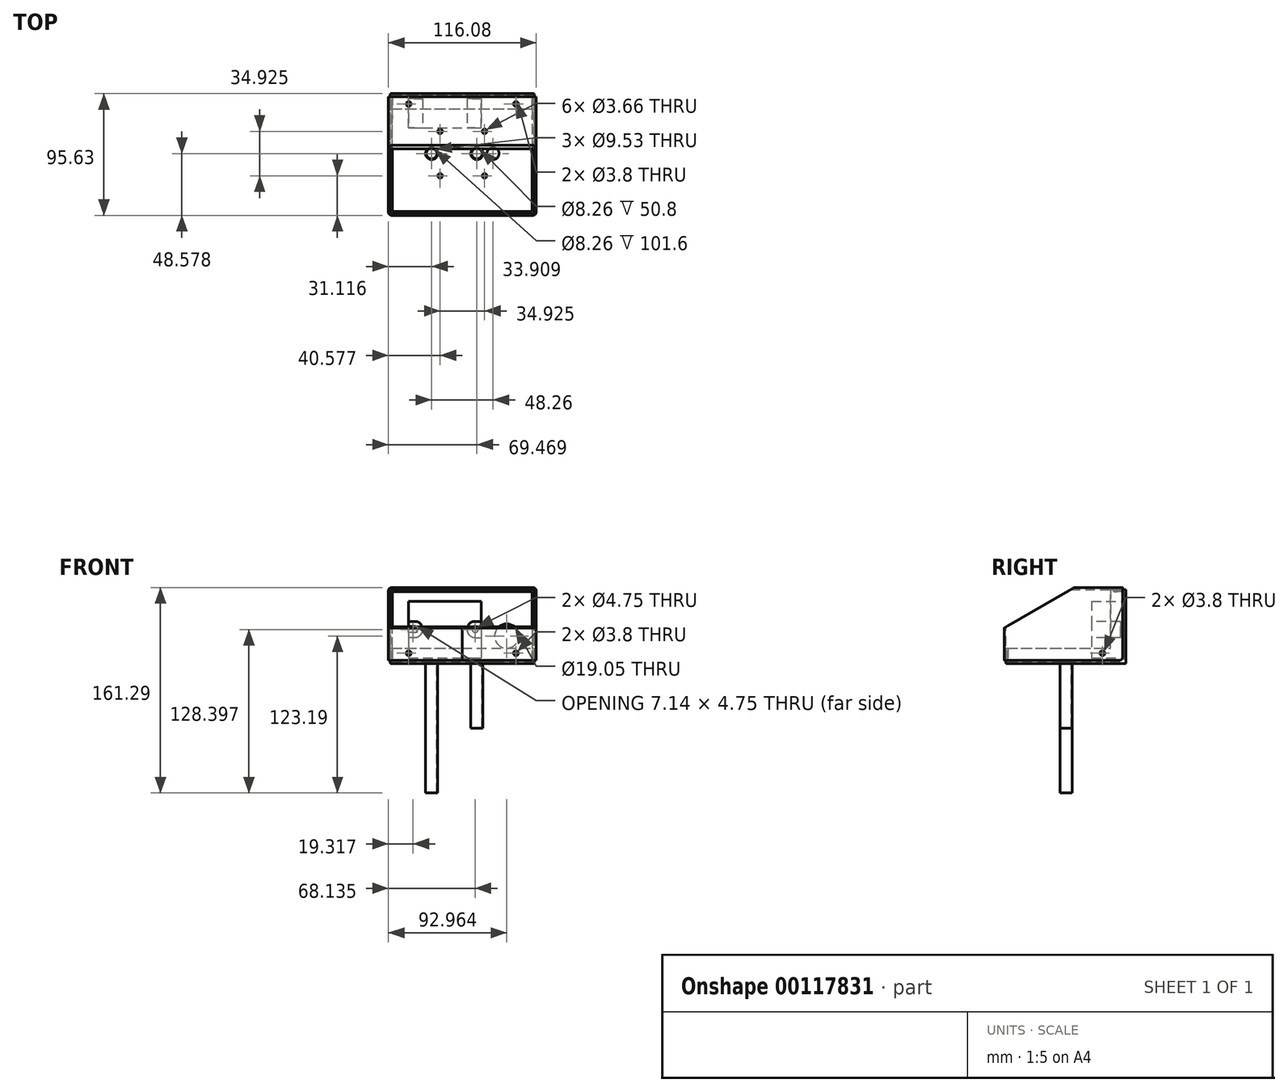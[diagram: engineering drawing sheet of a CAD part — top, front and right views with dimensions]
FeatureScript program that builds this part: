
annotation { "Feature Type Name" : "Feature", "Feature Type Description" : "" }
export const myFeature = defineFeature(function(context is Context, id is Id, definition is map)
    precondition{}
    {
        {
            var Q0;
            Q0=qCreatedBy(makeId("Right.planeOp"),FACE);
            var sketch = newSketch(context, id + "F0", { "sketchPlane" : qUnion([Q0])});
            skLineSegment(sketch, "E0", {"start": v(0, 0) * mm, "end": v(0, 25.4) * mm});
            skLineSegment(sketch, "E1", {"start": v(0, 25.4) * mm, "end": v(55, 57.15) * mm});
            skLineSegment(sketch, "E2", {"start": v(55, 57.15) * mm, "end": v(93.1, 57.15) * mm});
            skLineSegment(sketch, "E3", {"start": v(93.1, 57.15) * mm, "end": v(93.1, 0) * mm});
            skLineSegment(sketch, "E4", {"start": v(93.1, 0) * mm, "end": v(0, 0) * mm});
            skSolve(sketch);
        }
        {
            var Q0;
            Q0 = qSketchRegion(id + "F0", true);
            extrude(context, id + "F1", {"entities" : qUnion([Q0]), "depth" : 116.08 * mm});
        }
        {
            var Q0;
            Q0=makeQuery(id+"F1.opExtrude","CAP_EDGE",EDGE,{"disambiguationData":[OSD([sQuery(id+"F0.wireOp",EDGE,"E2")])],"isStart":false});
            var Q1;
            Q1=makeQuery(id+"F1.opExtrude","CAP_EDGE",EDGE,{"disambiguationData":[OSD([sQuery(id+"F0.wireOp",EDGE,"E0")])],"isStart":false});
            var Q2;
            Q2=makeQuery(id+"F1.opExtrude","CAP_EDGE",EDGE,{"disambiguationData":[OSD([sQuery(id+"F0.wireOp",EDGE,"E0")])],"isStart":true});
            var Q3;
            Q3=makeQuery(id+"F1.opExtrude","CAP_EDGE",EDGE,{"disambiguationData":[OSD([sQuery(id+"F0.wireOp",EDGE,"E2")])],"isStart":true});
            fillet(context, id + "F2", {"entities" : qUnion([Q0, Q1, Q2, Q3]), "radius" : 2.54 * mm, "tangentPropagation" : true, "allowEdgeOverflow" : false});
        }
        {
            var Q0;
            Q0=makeQuery(id+"F1.opExtrude","SWEPT_FACE",FACE,{"disambiguationData":[OSD([sQuery(id+"F0.wireOp",EDGE,"E3")])]});
            var Q1;
            Q1=makeQuery(id+"F1.opExtrude","SWEPT_FACE",FACE,{"disambiguationData":[OSD([sQuery(id+"F0.wireOp",EDGE,"E4")])]});
            var Q2;
            Q2=makeQuery(id+"F1.opExtrude","SWEPT_FACE",FACE,{"disambiguationData":[OSD([sQuery(id+"F0.wireOp",EDGE,"E1")])]});
            shell(context, id + "F3", {"entities" : qUnion([Q0, Q1, Q2]), "thickness" : 1.52 * mm});
        }
        {
            var Q0;
            {var subQ0=sQuery(id+"F0.wireOp",EDGE,"E4");var subQ1=sQuery(id+"F0.wireOp",EDGE,"E3");var subQ2=sQuery(id+"F0.wireOp",EDGE,"E2");var subQ3=sQuery(id+"F0.wireOp",EDGE,"E1");var subQ4=sQuery(id+"F0.wireOp",EDGE,"E0");Q0=makeQuery(id+"F3.opShell","OFFSET_FACE",FACE,{"disambiguationData":[OSD([subQ4,subQ3,subQ2,subQ1,subQ0]),TDD([makeQuery(id+"F1.opExtrude","CAP_FACE",FACE,{"disambiguationData":[OSD([subQ4,subQ3,subQ2,subQ1,subQ0])],"isStart":false})])]});}
            var sketch = newSketch(context, id + "F4", { "sketchPlane" : qUnion([Q0])});
            skLineSegment(sketch, "E5.0", {"start": v(-93.1, 0) * mm, "end": v(-1.52, 0) * mm, "construction": true});
            skLineSegment(sketch, "E5.1", {"start": v(-93.1, 55.63) * mm, "end": v(-93.1, 0) * mm, "construction": true});
            skLineSegment(sketch, "E6.0", {"start": v(-83.57, 9.53) * mm, "end": v(-1.52, 9.53) * mm});
            skLineSegment(sketch, "E6.1", {"start": v(-83.57, 55.63) * mm, "end": v(-83.57, 9.53) * mm});
            skLineSegment(sketch, "E7", {"start": v(-83.57, 55.63) * mm, "end": v(-93.1, 55.63) * mm});
            skLineSegment(sketch, "E8", {"start": v(-1.52, 0) * mm, "end": v(-1.52, 9.53) * mm});
            skLineSegment(sketch, "E9.0", {"start": v(-95.63, -2.54) * mm, "end": v(-1.52, -2.54) * mm});
            skLineSegment(sketch, "E9.1", {"start": v(-95.63, 55.63) * mm, "end": v(-95.63, -2.54) * mm});
            skLineSegment(sketch, "E10", {"start": v(-95.63, 55.63) * mm, "end": v(-93.1, 55.63) * mm});
            skLineSegment(sketch, "E11", {"start": v(-1.52, -2.54) * mm, "end": v(-1.52, 0) * mm});
            skSolve(sketch);
        }
        {
            var Q0;
            Q0 = qSketchRegion(id + "F4", true);
            var Q1;
            {var subQ0=sQuery(id+"F0.wireOp",EDGE,"E4");var subQ1=sQuery(id+"F0.wireOp",EDGE,"E3");var subQ2=sQuery(id+"F0.wireOp",EDGE,"E2");var subQ3=sQuery(id+"F0.wireOp",EDGE,"E1");var subQ4=sQuery(id+"F0.wireOp",EDGE,"E0");Q1=makeQuery(id+"F3.opShell","OFFSET_FACE",FACE,{"disambiguationData":[OSD([subQ4,subQ3,subQ2,subQ1,subQ0]),TDD([makeQuery(id+"F1.opExtrude","CAP_FACE",FACE,{"disambiguationData":[OSD([subQ4,subQ3,subQ2,subQ1,subQ0])],"isStart":true})])]});}
            var Q2;
            Q2=makeQuery(id+"F1.opExtrude","SWEPT_BODY",BODY,{"disambiguationData":[OSD([sQuery(id+"F0.wireOp",EDGE,"E0"),sQuery(id+"F0.wireOp",EDGE,"E1"),sQuery(id+"F0.wireOp",EDGE,"E2"),sQuery(id+"F0.wireOp",EDGE,"E3"),sQuery(id+"F0.wireOp",EDGE,"E4")])]});
            extrude(context, id + "F5", {"entities" : qUnion([Q0]), "endBound" : BoundingType.UP_TO_SURFACE, "endBoundEntityFace" : qUnion([Q1]), "endBoundEntityBody" : qUnion([Q2]), "depth" : 25.4 * mm});
        }
        {
            var Q0;
            Q0=makeQuery(id+"F5.opExtrude","SWEPT_FACE",FACE,{"disambiguationData":[OSD([sQuery(id+"F4.wireOp",EDGE,"E6.1")])]});
            var Q1;
            Q1=makeQuery(id+"F5.opExtrude","SWEPT_FACE",FACE,{"disambiguationData":[OSD([sQuery(id+"F4.wireOp",EDGE,"E6.0")])]});
            shell(context, id + "F6", {"entities" : qUnion([Q0, Q1]), "thickness" : 1.52 * mm});
        }
        {
            var Q0;
            {var subQ0=sQuery(id+"F4.wireOp",EDGE,"E9.1");Q0=makeQuery(id+"F6.opShell","OFFSET_FACE",FACE,{"disambiguationData":[OSD([subQ0]),TDD([makeQuery(id+"F5.opExtrude","SWEPT_FACE",FACE,{"disambiguationData":[OSD([subQ0])]})])]});}
            var sketch = newSketch(context, id + "F7", { "sketchPlane" : qUnion([Q0])});
            skLineSegment(sketch, "E12.bottom", {"start": v(15.75, 46.48) * mm, "end": v(72.9, 46.48) * mm});
            skLineSegment(sketch, "E12.top", {"start": v(15.75, 2.03) * mm, "end": v(72.9, 2.03) * mm});
            skLineSegment(sketch, "E12.left", {"start": v(15.75, 46.48) * mm, "end": v(15.75, 2.03) * mm});
            skLineSegment(sketch, "E12.right", {"start": v(72.9, 46.48) * mm, "end": v(72.9, 2.03) * mm});
            skSolve(sketch);
        }
        {
            var Q0;
            Q0 = qSketchRegion(id + "F7", true);
            extrude(context, id + "F8", {"entities" : qUnion([Q0]), "depth" : 25.4 * mm});
        }
        {
            var Q0;
            Q0=makeQuery(id+"F8.opExtrude","CAP_FACE",FACE,{"disambiguationData":[OSD([sQuery(id+"F7.wireOp",EDGE,"E12.bottom"),sQuery(id+"F7.wireOp",EDGE,"E12.top"),sQuery(id+"F7.wireOp",EDGE,"E12.left"),sQuery(id+"F7.wireOp",EDGE,"E12.right")])],"isStart":false});
            var sketch = newSketch(context, id + "F9", { "sketchPlane" : qUnion([Q0])});
            skArc(sketch, "E13", {"start": v(68.14, 30.6) * mm, "mid": v(61.79, 24.26) * mm, "end": v(68.14, 17.9) * mm});
            skPoint(sketch, "E13.centerSnap0", {"position": v(72.9, 24.26) * mm});
            skLineSegment(sketch, "E14", {"start": v(44.32, 46.48) * mm, "end": v(44.32, 2.03) * mm, "construction": true});
            skLineSegment(sketch, "E15", {"start": v(68.14, 30.6) * mm, "end": v(72.9, 30.6) * mm});
            skLineSegment(sketch, "E16", {"start": v(68.14, 17.9) * mm, "end": v(72.9, 17.9) * mm});
            skLineSegment(sketch, "E17", {"start": v(72.9, 17.9) * mm, "end": v(72.9, 30.6) * mm});
            skLineSegment(sketch, "E18.MirrorCS", {"start": v(20.51, 30.6) * mm, "end": v(15.75, 30.6) * mm});
            skLineSegment(sketch, "E19.MirrorCS", {"start": v(20.51, 17.9) * mm, "end": v(15.75, 17.9) * mm});
            skLineSegment(sketch, "E20.MirrorCS", {"start": v(15.75, 17.9) * mm, "end": v(15.75, 30.6) * mm});
            skArc(sketch, "E21.MirrorCS", {"start": v(20.51, 30.6) * mm, "mid": v(26.86, 24.26) * mm, "end": v(20.51, 17.9) * mm});
            skSolve(sketch);
        }
        {
            var Q0;
            Q0 = qSketchRegion(id + "F9", true);
            extrude(context, id + "F10", {"entities" : qUnion([Q0]), "operationType" : NewBodyOperationType.REMOVE, "oppositeDirection" : true, "depth" : 22.86 * mm});
        }
        {
            var Q0;
            Q0=makeQuery(id+"F8.opExtrude","CAP_FACE",FACE,{"disambiguationData":[OSD([sQuery(id+"F7.wireOp",EDGE,"E12.bottom"),sQuery(id+"F7.wireOp",EDGE,"E12.top"),sQuery(id+"F7.wireOp",EDGE,"E12.left"),sQuery(id+"F7.wireOp",EDGE,"E12.right")])],"isStart":false});
            var sketch = newSketch(context, id + "F11", { "sketchPlane" : qUnion([Q0])});
            skArc(sketch, "E22", {"start": v(20.51, 21.88) * mm, "mid": v(22.89, 24.26) * mm, "end": v(20.51, 26.63) * mm});
            skLineSegment(sketch, "E23", {"start": v(20.51, 26.63) * mm, "end": v(15.75, 26.63) * mm});
            skLineSegment(sketch, "E24", {"start": v(20.51, 21.88) * mm, "end": v(15.75, 21.88) * mm});
            skLineSegment(sketch, "E25", {"start": v(15.75, 21.88) * mm, "end": v(15.75, 26.63) * mm});
            skCircle(sketch, "E26", {"center": v(68.14, 24.26) * mm, "radius": 2.37 * mm});
            skSolve(sketch);
        }
        {
            var Q0;
            Q0 = qSketchRegion(id + "F11", true);
            extrude(context, id + "F12", {"entities" : qUnion([Q0]), "operationType" : NewBodyOperationType.REMOVE, "endBound" : BoundingType.THROUGH_ALL, "oppositeDirection" : true, "depth" : 25.4 * mm});
        }
        {
            var Q0;
            Q0=makeQuery(id+"F5.opExtrude","SWEPT_FACE",FACE,{"disambiguationData":[OSD([sQuery(id+"F4.wireOp",EDGE,"E9.0")])]});
            var sketch = newSketch(context, id + "F13", { "sketchPlane" : qUnion([Q0])});
            skCircle(sketch, "E27", {"center": v(82.17, -48.58) * mm, "radius": 4.76 * mm});
            skCircle(sketch, "E28", {"center": v(69.47, -48.58) * mm, "radius": 4.76 * mm});
            skLineSegment(sketch, "E29", {"start": v(58.04, -93.1) * mm, "end": v(58.04, -4.06) * mm, "construction": true});
            skCircle(sketch, "E30", {"center": v(33.9, -48.58) * mm, "radius": 4.76 * mm});
            skPoint(sketch, "E31", {"position": v(58.04, -48.58) * mm});
            skSolve(sketch);
        }
        {
            var Q0;
            Q0 = qSketchRegion(id + "F13", true);
            extrude(context, id + "F14", {"entities" : qUnion([Q0]), "operationType" : NewBodyOperationType.REMOVE, "endBound" : BoundingType.UP_TO_NEXT, "oppositeDirection" : true, "depth" : 25.4 * mm});
        }
        {
            var Q0;
            Q0=makeQuery(id+"F5.opExtrude","SWEPT_FACE",FACE,{"disambiguationData":[OSD([sQuery(id+"F4.wireOp",EDGE,"E9.0")])]});
            var sketch = newSketch(context, id + "F15", { "sketchPlane" : qUnion([Q0])});
            skCircle(sketch, "E32.0", {"center": v(33.9, -48.58) * mm, "radius": 4.76 * mm});
            skCircle(sketch, "E32.1", {"center": v(69.47, -48.58) * mm, "radius": 4.76 * mm});
            skCircle(sketch, "E33.0", {"center": v(69.47, -48.58) * mm, "radius": 4.13 * mm});
            skCircle(sketch, "E34.0", {"center": v(33.9, -48.58) * mm, "radius": 4.13 * mm});
            skSolve(sketch);
        }
        {
            var Q0;
            Q0=makeQuery(id+"F15.imprint","IMPRINT",FACE,{"disambiguationData":[TD([[makeQuery(id+"F15.imprint","IMPRINT",EDGE,{"derivedFrom":sQuery(id+"F15.wireOp",EDGE,"E32.1")}),1.0]])]});
            extrude(context, id + "F16", {"entities" : qUnion([Q0]), "depth" : 50.8 * mm});
        }
        {
            var Q0;
            Q0=makeQuery(id+"F15.imprint","IMPRINT",FACE,{"disambiguationData":[TD([[makeQuery(id+"F15.imprint","IMPRINT",EDGE,{"derivedFrom":sQuery(id+"F15.wireOp",EDGE,"E32.0")}),1.0]])]});
            extrude(context, id + "F17", {"entities" : qUnion([Q0]), "depth" : 101.6 * mm});
        }
        {
            var Q0;
            Q0=makeQuery(id+"F13.imprint","IMPRINT",FACE,{"disambiguationData":[TD([[makeQuery(id+"F13.imprint","IMPRINT",EDGE,{"derivedFrom":sQuery(id+"F13.wireOp",EDGE,"E27")}),-1.0]])]});
            var sketch = newSketch(context, id + "F18", { "sketchPlane" : qUnion([Q0])});
            skLineSegment(sketch, "E35.bottom", {"start": v(75.5, -66.04) * mm, "end": v(40.58, -66.04) * mm, "construction": true});
            skLineSegment(sketch, "E35.top", {"start": v(75.5, -31.12) * mm, "end": v(40.58, -31.12) * mm, "construction": true});
            skLineSegment(sketch, "E35.left", {"start": v(75.5, -66.04) * mm, "end": v(75.5, -31.12) * mm, "construction": true});
            skLineSegment(sketch, "E35.right", {"start": v(40.58, -66.04) * mm, "end": v(40.58, -31.12) * mm, "construction": true});
            skPoint(sketch, "E35.middle", {"position": v(58.04, -48.58) * mm});
            skCircle(sketch, "E36", {"center": v(40.58, -31.12) * mm, "radius": 1.83 * mm});
            skCircle(sketch, "E37", {"center": v(75.5, -31.12) * mm, "radius": 1.83 * mm});
            skCircle(sketch, "E38", {"center": v(75.5, -66.04) * mm, "radius": 1.83 * mm});
            skCircle(sketch, "E39", {"center": v(40.58, -66.04) * mm, "radius": 1.83 * mm});
            skSolve(sketch);
        }
        {
            var Q0;
            Q0 = qSketchRegion(id + "F18", true);
            extrude(context, id + "F19", {"entities" : qUnion([Q0]), "operationType" : NewBodyOperationType.REMOVE, "endBound" : BoundingType.THROUGH_ALL, "oppositeDirection" : true, "depth" : 25.4 * mm});
        }
        {
            var Q0;
            {var subQ0=sQuery(id+"F4.wireOp",EDGE,"E9.1");Q0=makeQuery(id+"F6.opShell","OFFSET_FACE",FACE,{"disambiguationData":[OSD([subQ0]),TDD([makeQuery(id+"F5.opExtrude","SWEPT_FACE",FACE,{"disambiguationData":[OSD([subQ0])]})])]});}
            var sketch = newSketch(context, id + "F20", { "sketchPlane" : qUnion([Q0])});
            skCircle(sketch, "E40", {"center": v(20.51, 24.26) * mm, "radius": 2.15 * mm});
            skCircle(sketch, "E41", {"center": v(68.14, 24.26) * mm, "radius": 2.15 * mm});
            skSolve(sketch);
        }
        {
            var Q0;
            Q0 = qSketchRegion(id + "F20", true);
            extrude(context, id + "F21", {"entities" : qUnion([Q0]), "operationType" : NewBodyOperationType.REMOVE, "endBound" : BoundingType.THROUGH_ALL, "oppositeDirection" : true, "depth" : 25.4 * mm});
        }
        {
            var Q0;
            {var subQ0=sQuery(id+"F4.wireOp",EDGE,"E9.1");Q0=makeQuery(id+"F6.opShell","OFFSET_FACE",FACE,{"disambiguationData":[OSD([subQ0]),TDD([makeQuery(id+"F5.opExtrude","SWEPT_FACE",FACE,{"disambiguationData":[OSD([subQ0])]})])]});}
            var sketch = newSketch(context, id + "F22", { "sketchPlane" : qUnion([Q0])});
            skCircle(sketch, "E42", {"center": v(92.96, 19.05) * mm, "radius": 9.53 * mm});
            skSolve(sketch);
        }
        {
            var Q0;
            Q0=makeQuery(id+"F22.imprint","IMPRINT",FACE,{"disambiguationData":[TD([[makeQuery(id+"F22.imprint","IMPRINT",EDGE,{"derivedFrom":sQuery(id+"F22.wireOp",EDGE,"E42")}),1.0]])]});
            extrude(context, id + "F23", {"entities" : qUnion([Q0]), "operationType" : NewBodyOperationType.REMOVE, "endBound" : BoundingType.THROUGH_ALL, "oppositeDirection" : true, "depth" : 25.4 * mm});
        }
        {
            var Q0;
            Q0=makeQuery(id+"F1.opExtrude","CAP_FACE",FACE,{"disambiguationData":[OSD([sQuery(id+"F0.wireOp",EDGE,"E0"),sQuery(id+"F0.wireOp",EDGE,"E1"),sQuery(id+"F0.wireOp",EDGE,"E2"),sQuery(id+"F0.wireOp",EDGE,"E3"),sQuery(id+"F0.wireOp",EDGE,"E4")])],"isStart":true});
            var sketch = newSketch(context, id + "F24", { "sketchPlane" : qUnion([Q0])});
            skLineSegment(sketch, "E43", {"start": v(-77.22, 0) * mm, "end": v(-77.22, 9.53) * mm, "construction": true});
            skPoint(sketch, "E44", {"position": v(-77.22, 5.59) * mm});
            skSolve(sketch);
        }
        {
            var Q0;
            Q0=makeQuery(id+"F1.opExtrude","SWEPT_FACE",FACE,{"disambiguationData":[OSD([sQuery(id+"F0.wireOp",EDGE,"E0")])]});
            var sketch = newSketch(context, id + "F25", { "sketchPlane" : qUnion([Q0])});
            skLineSegment(sketch, "E45", {"start": v(15.88, 0) * mm, "end": v(15.88, 9.53) * mm, "construction": true});
            skPoint(sketch, "E46", {"position": v(15.88, 5.59) * mm});
            skLineSegment(sketch, "E47", {"start": v(58.04, 0) * mm, "end": v(58.04, 69.33) * mm, "construction": true});
            skPoint(sketch, "E47.endSnap0", {"position": v(58.04, 25.4) * mm});
            skPoint(sketch, "E48.MirrorP", {"position": v(100.2, 5.59) * mm});
            skSolve(sketch);
        }
        {
            var Q0;
            Q0=makeQuery(id+"F1.opExtrude","SWEPT_FACE",FACE,{"disambiguationData":[OSD([sQuery(id+"F0.wireOp",EDGE,"E2")])]});
            var sketch = newSketch(context, id + "F26", { "sketchPlane" : qUnion([Q0])});
            skLineSegment(sketch, "E49", {"start": v(100.2, 93.1) * mm, "end": v(100.2, 83.57) * mm, "construction": true});
            skLineSegment(sketch, "E50", {"start": v(15.87, 93.1) * mm, "end": v(15.87, 83.57) * mm, "construction": true});
            skPoint(sketch, "E51", {"position": v(15.87, 87.5) * mm});
            skPoint(sketch, "E52", {"position": v(100.2, 87.5) * mm});
            skSolve(sketch);
        }
        {
            var Q0;
            Q0=sQuery(id+"F26.wireOp",VERTEX,"E52");
            var Q1;
            Q1=sQuery(id+"F26.wireOp",VERTEX,"E51");
            var Q2;
            Q2=sQuery(id+"F25.wireOp",VERTEX,"E46");
            var Q3;
            Q3=sQuery(id+"F24.wireOp",VERTEX,"E44");
            var Q4;
            Q4=sQuery(id+"F25.wireOp",VERTEX,"E48.MirrorP");
            var Q5;
            Q5=makeQuery(id+"F1.opExtrude","SWEPT_BODY",BODY,{"disambiguationData":[OSD([sQuery(id+"F0.wireOp",EDGE,"E0"),sQuery(id+"F0.wireOp",EDGE,"E1"),sQuery(id+"F0.wireOp",EDGE,"E2"),sQuery(id+"F0.wireOp",EDGE,"E3"),sQuery(id+"F0.wireOp",EDGE,"E4")])]});
            hole(context, id + "F27", {"style" : HoleStyle.SIMPLE, "endStyle" : HoleEndStyle.THROUGH, "standardTappedOrClearance" : lookupTablePath({ "standard" : "ANSI", "fit" : "Normal (ASME)", "size" : "#6", "type" : "Clearance" }), "standardBlindInLast" : lookupTablePath({ "fit" : "Free", "standard" : "ANSI", "size" : "#6", "type" : "Clearance" }), "holeDiameter" : 3.8 * mm, "locations" : qUnion([Q0, Q1, Q2, Q3, Q4]), "scope" : qUnion([Q5]), "isTappedThrough" : true});
        }
        {
            var Q0;
            Q0=sQuery(id+"F24.wireOp",VERTEX,"E44");
            var Q1;
            Q1=makeQuery(id+"F5.opExtrude","SWEPT_BODY",BODY,{"disambiguationData":[OSD([sQuery(id+"F4.wireOp",EDGE,"E6.0"),sQuery(id+"F4.wireOp",EDGE,"E6.1"),sQuery(id+"F4.wireOp",EDGE,"E7"),sQuery(id+"F4.wireOp",EDGE,"E8"),sQuery(id+"F4.wireOp",EDGE,"E9.0"),sQuery(id+"F4.wireOp",EDGE,"E9.1"),sQuery(id+"F4.wireOp",EDGE,"E10"),sQuery(id+"F4.wireOp",EDGE,"E11")])]});
            hole(context, id + "F28", {"style" : HoleStyle.SIMPLE, "endStyle" : HoleEndStyle.THROUGH, "standardTappedOrClearance" : lookupTablePath({ "standard" : "ANSI", "fit" : "Normal (ASME)", "engagement" : "75%", "pitch" : "32 tpi", "size" : "#6", "type" : "Tapped" }), "standardBlindInLast" : lookupTablePath({ "fit" : "Free", "standard" : "ANSI", "engagement" : "75%", "pitch" : "32 tpi", "size" : "#6", "type" : "Tapped" }), "holeDiameter" : 2.7 * mm, "locations" : qUnion([Q0]), "scope" : qUnion([Q1]), "isTappedThrough" : true, "majorDiameter" : 3.5 * mm, "showTappedDepth" : true});
        }
        {
            var Q0;
            Q0=sQuery(id+"F26.wireOp",VERTEX,"E51");
            var Q1;
            Q1=sQuery(id+"F26.wireOp",VERTEX,"E52");
            var Q2;
            Q2=sQuery(id+"F25.wireOp",VERTEX,"E48.MirrorP");
            var Q3;
            Q3=sQuery(id+"F25.wireOp",VERTEX,"E46");
            var Q4;
            Q4=makeQuery(id+"F5.opExtrude","SWEPT_BODY",BODY,{"disambiguationData":[OSD([sQuery(id+"F4.wireOp",EDGE,"E6.0"),sQuery(id+"F4.wireOp",EDGE,"E6.1"),sQuery(id+"F4.wireOp",EDGE,"E7"),sQuery(id+"F4.wireOp",EDGE,"E8"),sQuery(id+"F4.wireOp",EDGE,"E9.0"),sQuery(id+"F4.wireOp",EDGE,"E9.1"),sQuery(id+"F4.wireOp",EDGE,"E10"),sQuery(id+"F4.wireOp",EDGE,"E11")])]});
            hole(context, id + "F29", {"style" : HoleStyle.SIMPLE, "endStyle" : HoleEndStyle.BLIND, "standardTappedOrClearance" : lookupTablePath({ "standard" : "ANSI", "fit" : "Normal (ASME)", "engagement" : "75%", "pitch" : "32 tpi", "size" : "#6", "type" : "Tapped" }), "standardBlindInLast" : lookupTablePath({ "fit" : "Free", "standard" : "ANSI", "engagement" : "75%", "pitch" : "32 tpi", "size" : "#6", "type" : "Tapped" }), "holeDiameter" : 2.7 * mm, "holeDepth" : 12.7 * mm, "locations" : qUnion([Q0, Q1, Q2, Q3]), "scope" : qUnion([Q4]), "majorDiameter" : 3.5 * mm});
        }
        {
            var Q0;
            Q0=makeQuery(id+"F1.opExtrude","SWEPT_FACE",FACE,{"disambiguationData":[OSD([sQuery(id+"F0.wireOp",EDGE,"E0")])]});
            var sketch = newSketch(context, id + "F30", { "sketchPlane" : qUnion([Q0])});
            skLineSegment(sketch, "E53", {"start": v(58.04, 0) * mm, "end": v(58.04, 69.69) * mm});
            skLineSegment(sketch, "E54.0", {"start": v(58.06, 0) * mm, "end": v(58.06, 69.69) * mm});
            skLineSegment(sketch, "E55", {"start": v(58.04, 69.69) * mm, "end": v(58.06, 69.69) * mm});
            skLineSegment(sketch, "E56", {"start": v(58.04, 0) * mm, "end": v(58.06, 0) * mm});
            skSolve(sketch);
        }
        {
            var Q0;
            Q0 = qSketchRegion(id + "F30", true);
            extrude(context, id + "F31", {"entities" : qUnion([Q0]), "operationType" : NewBodyOperationType.REMOVE, "oppositeDirection" : true, "depth" : 25.4 * mm});
        }
        {
            var Q0;
            Q0=makeQuery(id+"F3.opShell","OFFSET_EDGE",EDGE,{"disambiguationData":[OSD([sQuery(id+"F0.wireOp",EDGE,"E3"),sQuery(id+"F0.wireOp",EDGE,"E4")])]});
            var Q1;
            Q1=makeQuery(id+"F1.opExtrude","SWEPT_EDGE",EDGE,{"disambiguationData":[OSD([sQuery(id+"F0.wireOp",EDGE,"E3"),sQuery(id+"F0.wireOp",EDGE,"E4")])]});
            fillet(context, id + "F32", {"entities" : qUnion([Q0, Q1]), "radius" : 2.54 * mm, "tangentPropagation" : true, "allowEdgeOverflow" : false});
        }
    });
